# Revit family: DBLTD_TheSenatorGroup_OfficeChairs_Colab_Seating_Corner_US
name_source: partatom
category: Furniture
units: mm (PartAtom-declared; Revit-internal decimal feet)

## family parameters
Always vertical = Yes
Cut with Voids When Loaded = No
OmniClass Number = 23.40.20.00
OmniClass Title = General Furniture and Specialties
Room Calculation Point = No
Shared = Yes
Work Plane-Based = No

## types (2) — shared parameters
Assembly Code = E2020200
AssetType = Movable
Category = Pr_40_50_12_57 Office chairs
Color = Seat & Back: Fully Upholstered. Frame: Smoke Grey Powder Coat. Shelf: Available in Senator
standard 25mm MFC finishes.
Constituents = Upholstered Seat and Back, Steel Frame
Default Elevation = 0"
DurationUnit = years
ExpectedLife = 5
Finish = Seat & Back: Fully Upholstered. Frame: Smoke Grey Powder Coat. Shelf: Available in Senator
standard 25mm MFC finishes.
Keynote = Pr_40_50_12_57 Office chairs
Manufacturer = The Senator Group
ManufacturerName = The Senator Group
ManufacturerURL = https://www.senator.online
Material = Seat & Back: Fully Upholstered Wood Frame Construction with Foam. Frame: Steel. Shelf: MFC.
Name = Chair
ProductInformation = https://www.senator.online
SeatingHeight = 19"
Shape = Rectangular
URL = https://www.thesenatorgroup.com
Uniclass2015Code = Pr_40_50_12_57
Uniclass2015Title = Office chairs
Uniclass2015Version = Products v1.15
Version = 1
WarrantyDescription = Senator warrants that its manufactured products are free from manufacturing defects - in materials or workmanship - for a period of ten (10) years on Senator Seating ranges; and fifteen (15) years on Senator Desking ranges
WarrantyDurationLabor = 5
WarrantyDurationParts = 5
WarrantyDurationUnit = years
WarrantyGuarantorLabor = https://www.thesenatorgroup.com
WarrantyGuarantorParts = https://www.thesenatorgroup.com
zero-valued in all types: Cost

## per-type parameters (varying)
| type | Model | ModelNumber | NominalDepth | NominalHeight | NominalWidth | ScreenType | SeatOffset | Size |
| Corner Chair | CB700B | CB700B | 97" | 31" | 97" | Nested_DBLTD_TheSenatorGroup_OfficeChairs_Colab_Seating_ScreenCorner : None | 0" | 96.85" x 96.85" x 31.50" |
| Corner Chair with Screens | CB700BS | CB700BS | 99" | 49" | 99" | Nested_DBLTD_TheSenatorGroup_OfficeChairs_Colab_Seating_ScreenCorner : Screen | 1" | 99.02" x 99.02" x 49.21" |

note: column(s) folded — value = type name in every type: Description, ModelReference, Type Comments

## geometry (parser evidence)
native form markers: Sweep x13
no freeform markers — native parametric forms only
